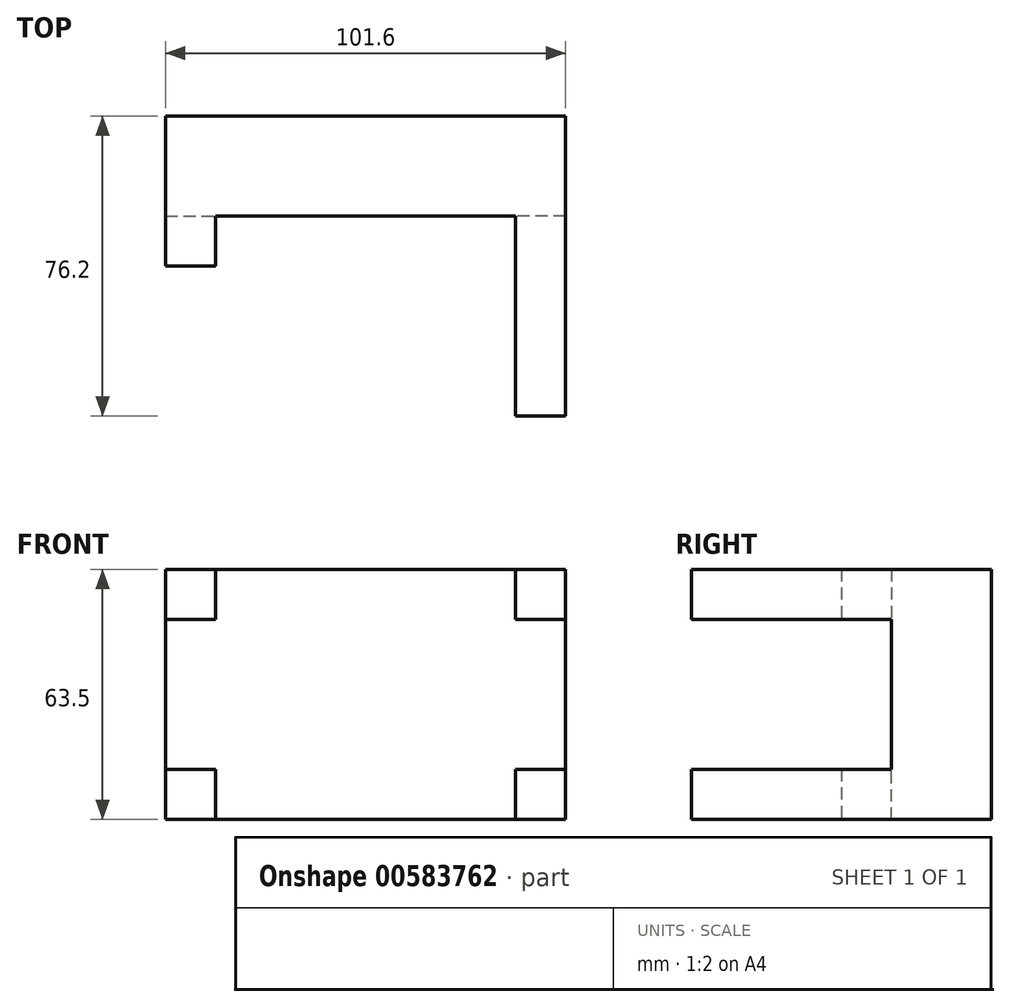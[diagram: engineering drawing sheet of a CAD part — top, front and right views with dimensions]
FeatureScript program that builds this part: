
annotation { "Feature Type Name" : "Feature", "Feature Type Description" : "" }
export const myFeature = defineFeature(function(context is Context, id is Id, definition is map)
    precondition{}
    {
        {
            var Q0;
            Q0=qCreatedBy(makeId("Front.planeOp"),FACE);
            var sketch = newSketch(context, id + "F0", { "sketchPlane" : qUnion([Q0])});
            skLineSegment(sketch, "E0.bottom", {"start": v(50.8, 31.75) * mm, "end": v(-50.8, 31.75) * mm});
            skLineSegment(sketch, "E0.top", {"start": v(50.8, -31.75) * mm, "end": v(-50.8, -31.75) * mm});
            skLineSegment(sketch, "E0.left", {"start": v(50.8, 31.75) * mm, "end": v(50.8, -31.75) * mm});
            skLineSegment(sketch, "E0.right", {"start": v(-50.8, 31.75) * mm, "end": v(-50.8, -31.75) * mm});
            skPoint(sketch, "E0.middle", {"position": v(0, 0) * mm});
            skSolve(sketch);
        }
        {
            var Q0;
            Q0=makeQuery(id+"F0.imprint","IMPRINT",FACE,{"disambiguationData":[TD([[makeQuery(id+"F0.imprint","IMPRINT",EDGE,{"derivedFrom":sQuery(id+"F0.wireOp",EDGE,"E0.bottom")}),1.0]])]});
            extrude(context, id + "F1", {"entities" : qUnion([Q0]), "depth" : 25.4 * mm, "offsetDistance" : 25.4 * mm});
        }
        {
            var Q0;
            Q0=makeQuery(id+"F1.opExtrude","CAP_FACE",FACE,{"disambiguationData":[OSD([sQuery(id+"F0.wireOp",EDGE,"E0.bottom"),sQuery(id+"F0.wireOp",EDGE,"E0.top"),sQuery(id+"F0.wireOp",EDGE,"E0.left"),sQuery(id+"F0.wireOp",EDGE,"E0.right")])],"isStart":false});
            var sketch = newSketch(context, id + "F2", { "sketchPlane" : qUnion([Q0])});
            skLineSegment(sketch, "E1.bottom", {"start": v(-50.8, 31.75) * mm, "end": v(-38.1, 31.75) * mm});
            skLineSegment(sketch, "E1.top", {"start": v(-50.8, 19.05) * mm, "end": v(-38.1, 19.05) * mm});
            skLineSegment(sketch, "E1.left", {"start": v(-50.8, 31.75) * mm, "end": v(-50.8, 19.05) * mm});
            skLineSegment(sketch, "E1.right", {"start": v(-38.1, 31.75) * mm, "end": v(-38.1, 19.05) * mm});
            skLineSegment(sketch, "E2.bottom", {"start": v(-50.8, -31.75) * mm, "end": v(-38.1, -31.75) * mm});
            skLineSegment(sketch, "E2.top", {"start": v(-50.8, -19.05) * mm, "end": v(-38.1, -19.05) * mm});
            skLineSegment(sketch, "E2.left", {"start": v(-50.8, -31.75) * mm, "end": v(-50.8, -19.05) * mm});
            skLineSegment(sketch, "E2.right", {"start": v(-38.1, -31.75) * mm, "end": v(-38.1, -19.05) * mm});
            skLineSegment(sketch, "E3.bottom", {"start": v(50.8, -31.75) * mm, "end": v(38.1, -31.75) * mm});
            skLineSegment(sketch, "E3.top", {"start": v(50.8, -19.05) * mm, "end": v(38.1, -19.05) * mm});
            skLineSegment(sketch, "E3.left", {"start": v(50.8, -31.75) * mm, "end": v(50.8, -19.05) * mm});
            skLineSegment(sketch, "E3.right", {"start": v(38.1, -31.75) * mm, "end": v(38.1, -19.05) * mm});
            skLineSegment(sketch, "E4.bottom", {"start": v(50.8, 31.75) * mm, "end": v(38.1, 31.75) * mm});
            skLineSegment(sketch, "E4.top", {"start": v(50.8, 19.05) * mm, "end": v(38.1, 19.05) * mm});
            skLineSegment(sketch, "E4.left", {"start": v(50.8, 31.75) * mm, "end": v(50.8, 19.05) * mm});
            skLineSegment(sketch, "E4.right", {"start": v(38.1, 31.75) * mm, "end": v(38.1, 19.05) * mm});
            skSolve(sketch);
        }
        {
            var Q0;
            Q0=makeQuery(id+"F2.imprint","IMPRINT",FACE,{"disambiguationData":[TD([[makeQuery(id+"F2.imprint","IMPRINT",EDGE,{"derivedFrom":sQuery(id+"F2.wireOp",EDGE,"E1.bottom")}),1.0]])]});
            var Q1;
            Q1=makeQuery(id+"F2.imprint","IMPRINT",FACE,{"disambiguationData":[TD([[makeQuery(id+"F2.imprint","IMPRINT",EDGE,{"derivedFrom":sQuery(id+"F2.wireOp",EDGE,"E2.bottom")}),-1.0]])]});
            extrude(context, id + "F3", {"entities" : qUnion([Q0, Q1]), "operationType" : NewBodyOperationType.ADD, "depth" : 12.7 * mm, "offsetDistance" : 25.4 * mm});
        }
        {
            var Q0;
            Q0=makeQuery(id+"F2.imprint","IMPRINT",FACE,{"disambiguationData":[TD([[makeQuery(id+"F2.imprint","IMPRINT",EDGE,{"derivedFrom":sQuery(id+"F2.wireOp",EDGE,"E4.bottom")}),1.0]])]});
            var Q1;
            Q1=makeQuery(id+"F2.imprint","IMPRINT",FACE,{"disambiguationData":[TD([[makeQuery(id+"F2.imprint","IMPRINT",EDGE,{"derivedFrom":sQuery(id+"F2.wireOp",EDGE,"E3.bottom")}),-1.0]])]});
            extrude(context, id + "F4", {"entities" : qUnion([Q0, Q1]), "operationType" : NewBodyOperationType.ADD, "depth" : 50.8 * mm, "offsetDistance" : 25.4 * mm});
        }
    });
